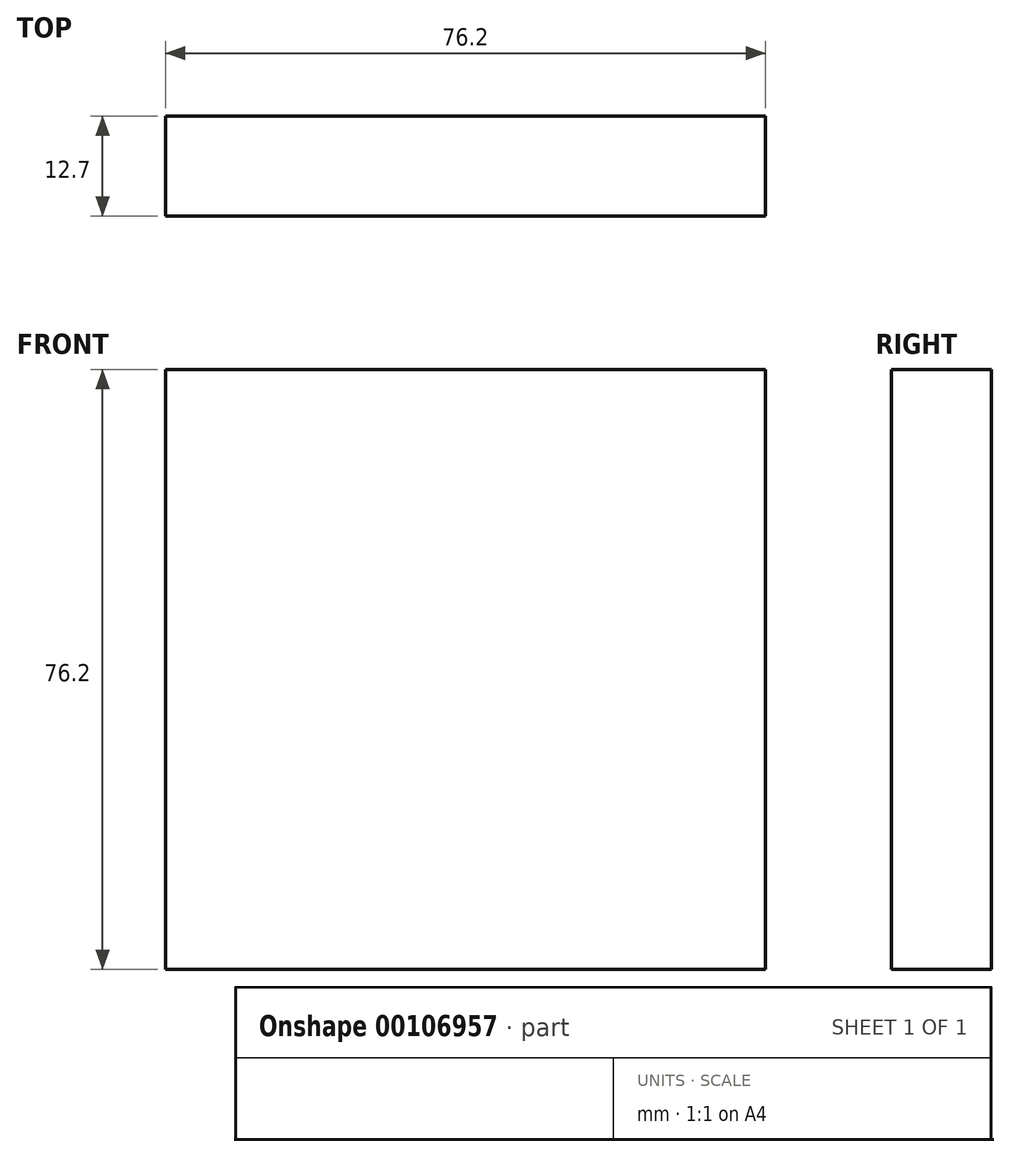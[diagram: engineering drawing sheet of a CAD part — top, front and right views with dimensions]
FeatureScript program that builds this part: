
annotation { "Feature Type Name" : "Feature", "Feature Type Description" : "" }
export const myFeature = defineFeature(function(context is Context, id is Id, definition is map)
    precondition{}
    {
        {
            var Q0;
            Q0=qCreatedBy(makeId("Front.planeOp"),FACE);
            var sketch = newSketch(context, id + "F0", { "sketchPlane" : qUnion([Q0])});
            skLineSegment(sketch, "E0.bottom", {"start": v(38.1, -38.1) * mm, "end": v(-38.1, -38.1) * mm});
            skLineSegment(sketch, "E0.top", {"start": v(38.1, 38.1) * mm, "end": v(-38.1, 38.1) * mm});
            skLineSegment(sketch, "E0.left", {"start": v(38.1, -38.1) * mm, "end": v(38.1, 38.1) * mm});
            skLineSegment(sketch, "E0.right", {"start": v(-38.1, -38.1) * mm, "end": v(-38.1, 38.1) * mm});
            skPoint(sketch, "E0.middle", {"position": v(0, 0) * mm});
            skSolve(sketch);
        }
        {
            var Q0;
            Q0 = qSketchRegion(id + "F0", true);
            extrude(context, id + "F1", {"entities" : qUnion([Q0]), "depth" : 12.7 * mm});
        }
    });
